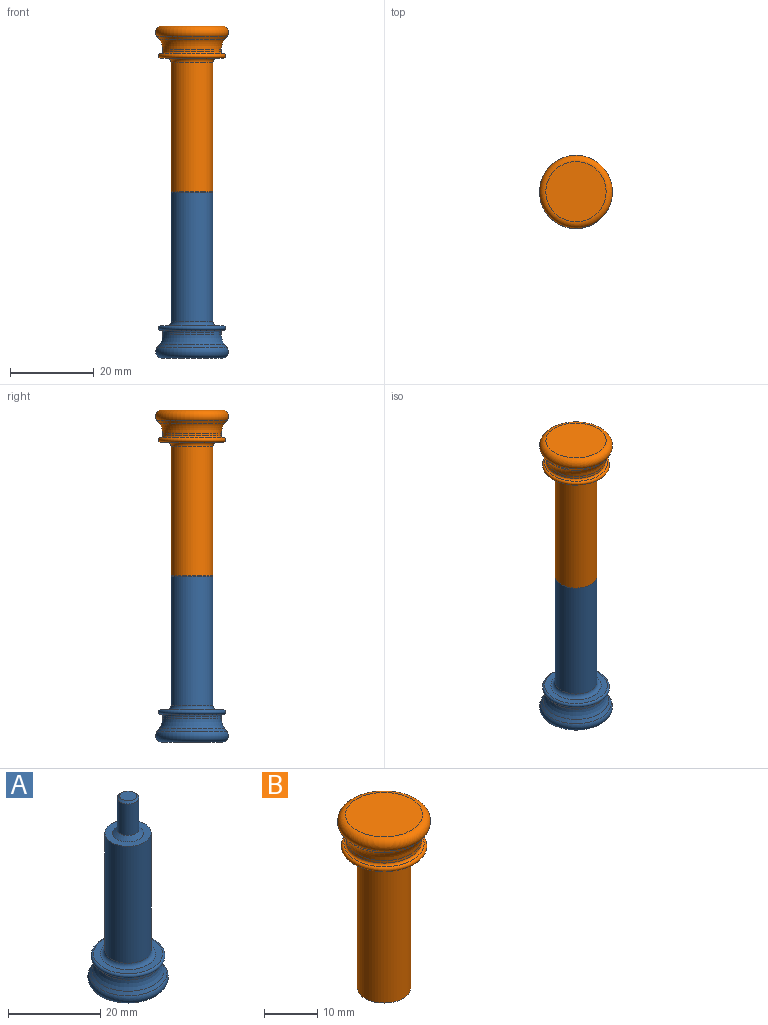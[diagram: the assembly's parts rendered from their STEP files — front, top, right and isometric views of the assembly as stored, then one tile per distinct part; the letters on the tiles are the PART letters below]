
ASSEMBLY  parts=2 mates=1
PART A: 15 faces, bbox 18.8x18.8x49.5 mm
  f0: plane 10x10mm, normal (0,0,1), area 43.3mm2, adj f1,f14
  f1: cylinder r=5mm len=31mm, axis (0,0,1), area 973.9mm2, adj f0,f2
  f2: torus R=6mm, axis (0,0,1), area 52.9mm2, adj f1,f3
  f3: plane 15x15mm, normal (0,0,1), area 63.6mm2, adj f2,f4
  f4: torus R=7.5mm, axis (0,0,1), area 77.2mm2, adj f3,f5
  f5: torus R=7.5mm, axis (0,0,1), area 35.4mm2, adj f4,f6
  f6: cylinder r=7mm len=14mm, axis (0,0,1), area 24.2mm2, adj f5,f7
  f7: torus R=11mm, axis (0,0,1), area 117.6mm2, adj f6,f8
  f8: cone r=7.8mm half-angle=36.9deg, axis (0,0,-1), area 50.9mm2, adj f7,f9
  f9: torus R=7.2mm, axis (0,0,1), area 172.9mm2, adj f8,f10
  f10: plane 14.4x14.4mm, normal (0,0,-1), area 162.9mm2, adj f9
  f11: cylinder r=2.35mm len=8.35mm, axis (0,0,-1), area 123.3mm2, adj f13,f14
  f12: plane 3.7x3.7mm, normal (0,0,1), area 10.8mm2, adj f13
  f13: cone r=1.85mm half-angle=45deg, axis (0,0,-1), area 9.3mm2, adj f11,f12
  f14: cone r=2.35mm half-angle=45deg, axis (0,0,-1), area 25.3mm2, adj f0,f11
PART B: 15 faces, bbox 18.8x18.8x39.6 mm
  f0: torus R=7.5mm, axis (0,0,1), area 35.4mm2, adj f1,f12
  f1: torus R=7.5mm, axis (0,0,1), area 77.2mm2, adj f0,f2
  f2: plane 15x15mm, normal (0,0,-1), area 63.6mm2, adj f1,f3
  f3: torus R=6mm, axis (0,0,1), area 52.9mm2, adj f2,f4
  f4: cylinder r=5mm len=31mm, axis (0,0,1), area 973.9mm2, adj f3,f5
  f5: plane 10x10mm, normal (0,0,-1), area 40.1mm2, adj f4,f13
  f6: cylinder r=2.5mm len=8.5mm, axis (0,0,1), area 133.5mm2, adj f13,f14
  f7: plane 4x4mm, normal (0,0,-1), area 12.6mm2, adj f14
  f8: plane 14.4x14.4mm, normal (0,0,1), area 162.9mm2, adj f9
  f9: torus R=7.2mm, axis (0,0,1), area 172.9mm2, adj f8,f10
  f10: cone r=7.8mm half-angle=36.9deg, axis (0,0,1), area 50.9mm2, adj f9,f11
  f11: torus R=11mm, axis (0,0,1), area 117.6mm2, adj f10,f12
  f12: cylinder r=7mm len=14mm, axis (0,0,1), area 24.2mm2, adj f0,f11
  f13: cone r=3.5mm half-angle=45deg, axis (0,0,-1), area 26.7mm2, adj f5,f6
  f14: cone r=2.5mm half-angle=45deg, axis (0,0,-1), area 10mm2, adj f6,f7
PLACE A t=(1.08,-14.06,17.39)mm
PLACE B t=(1.08,-8.71,7.59)mm
MATE revolute A.f11 <-> B.f0  axis (0,0,-1) through (1.08,-14.06,17.39)mm
